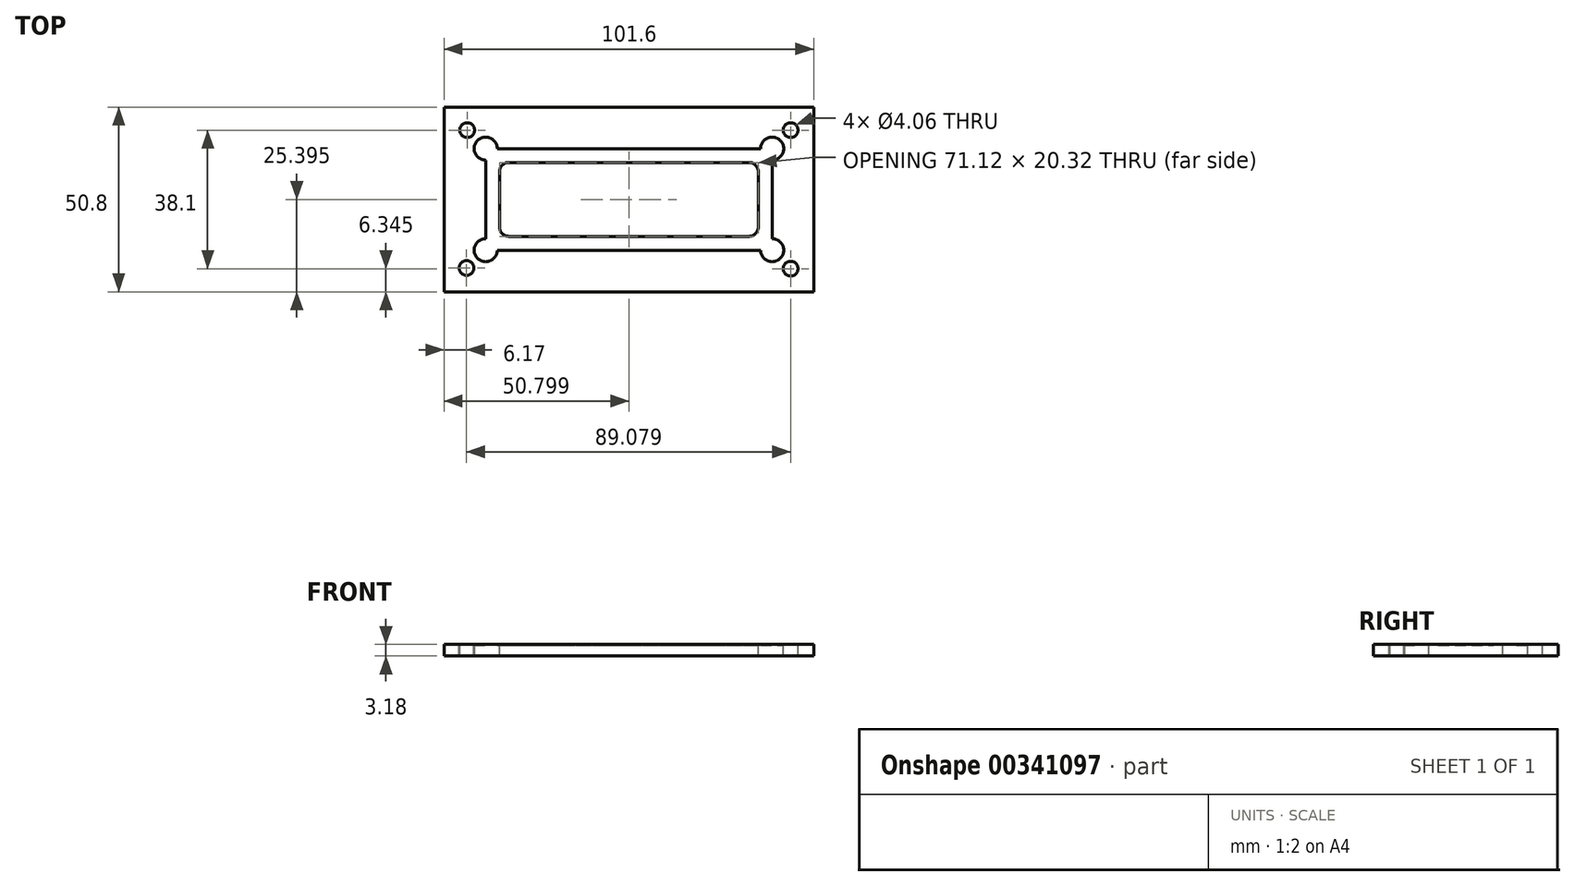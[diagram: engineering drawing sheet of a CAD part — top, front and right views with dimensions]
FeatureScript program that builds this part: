
annotation { "Feature Type Name" : "Feature", "Feature Type Description" : "" }
export const myFeature = defineFeature(function(context is Context, id is Id, definition is map)
    precondition{}
    {
        {
            var Q0;
            Q0=qCreatedBy(makeId("Top.planeOp"),FACE);
            var sketch = newSketch(context, id + "F0", { "sketchPlane" : qUnion([Q0])});
            skLineSegment(sketch, "E0.bottom", {"start": v(0.18, 50.6) * mm, "end": v(101.78, 50.6) * mm});
            skLineSegment(sketch, "E0.top", {"start": v(0.18, -0.2) * mm, "end": v(101.78, -0.2) * mm});
            skLineSegment(sketch, "E0.left", {"start": v(0.18, 50.6) * mm, "end": v(0.18, -0.2) * mm});
            skLineSegment(sketch, "E0.right", {"start": v(101.78, 50.6) * mm, "end": v(101.78, -0.2) * mm});
            skSolve(sketch);
        }
        {
            var Q0;
            Q0=makeQuery(id+"F0.imprint","IMPRINT",FACE,{"disambiguationData":[TD([[makeQuery(id+"F0.imprint","IMPRINT",EDGE,{"derivedFrom":sQuery(id+"F0.wireOp",EDGE,"E0.bottom")}),-1.0]])]});
            extrude(context, id + "F1", {"entities" : qUnion([Q0]), "depth" : 3.17 * mm});
        }
        {
            var Q0;
            Q0=makeQuery(id+"F1.opExtrude","CAP_FACE",FACE,{"disambiguationData":[OSD([sQuery(id+"F0.wireOp",EDGE,"E0.bottom"),sQuery(id+"F0.wireOp",EDGE,"E0.top"),sQuery(id+"F0.wireOp",EDGE,"E0.left"),sQuery(id+"F0.wireOp",EDGE,"E0.right")])],"isStart":false});
            var sketch = newSketch(context, id + "F2", { "sketchPlane" : qUnion([Q0])});
            skLineSegment(sketch, "E1.bottom", {"start": v(11.6, 39.17) * mm, "end": v(90.35, 39.17) * mm});
            skLineSegment(sketch, "E1.top", {"start": v(11.6, 11.23) * mm, "end": v(90.35, 11.23) * mm});
            skLineSegment(sketch, "E1.left", {"start": v(11.6, 39.17) * mm, "end": v(11.6, 11.23) * mm});
            skLineSegment(sketch, "E1.right", {"start": v(90.35, 39.17) * mm, "end": v(90.35, 11.23) * mm});
            skCircle(sketch, "E2", {"center": v(11.6, 39.17) * mm, "radius": 3.18 * mm});
            skCircle(sketch, "E3", {"center": v(11.6, 11.23) * mm, "radius": 3.18 * mm});
            skCircle(sketch, "E4", {"center": v(90.35, 39.17) * mm, "radius": 3.18 * mm});
            skCircle(sketch, "E5", {"center": v(90.35, 11.23) * mm, "radius": 3.18 * mm});
            skSolve(sketch);
        }
        {
            var Q0;
            {var subQ0=sQuery(id+"F2.wireOp",EDGE,"E1.left");var subQ1=sQuery(id+"F2.wireOp",EDGE,"E1.bottom");var subQ2=makeQuery(id+"F2.imprint","INTERSECT",VERTEX,{"derivedFrom":[subQ1,subQ0]});Q0=makeQuery(id+"F2.imprint","IMPRINT",FACE,{"disambiguationData":[TD([[makeQuery(id+"F2.imprint","IMPRINT",EDGE,{"disambiguationData":[TD([[subQ2,-1.0]])],"derivedFrom":subQ1}),1.0]])]});}
            var Q1;
            {var subQ0=sQuery(id+"F2.wireOp",EDGE,"E1.left");var subQ1=sQuery(id+"F2.wireOp",EDGE,"E1.bottom");var subQ2=makeQuery(id+"F2.imprint","INTERSECT",VERTEX,{"derivedFrom":[subQ1,subQ0]});Q1=makeQuery(id+"F2.imprint","IMPRINT",FACE,{"disambiguationData":[TD([[makeQuery(id+"F2.imprint","IMPRINT",EDGE,{"disambiguationData":[TD([[subQ2,-1.0]])],"derivedFrom":subQ1}),-1.0]])]});}
            var Q2;
            {var subQ0=sQuery(id+"F2.wireOp",EDGE,"E1.left");var subQ1=sQuery(id+"F2.wireOp",EDGE,"E1.top");var subQ2=makeQuery(id+"F2.imprint","INTERSECT",VERTEX,{"derivedFrom":[subQ1,subQ0]});Q2=makeQuery(id+"F2.imprint","IMPRINT",FACE,{"disambiguationData":[TD([[makeQuery(id+"F2.imprint","IMPRINT",EDGE,{"disambiguationData":[TD([[subQ2,-1.0]])],"derivedFrom":subQ1}),1.0]])]});}
            var Q3;
            {var subQ0=sQuery(id+"F2.wireOp",EDGE,"E1.left");var subQ1=sQuery(id+"F2.wireOp",EDGE,"E1.top");var subQ2=makeQuery(id+"F2.imprint","INTERSECT",VERTEX,{"derivedFrom":[subQ1,subQ0]});Q3=makeQuery(id+"F2.imprint","IMPRINT",FACE,{"disambiguationData":[TD([[makeQuery(id+"F2.imprint","IMPRINT",EDGE,{"disambiguationData":[TD([[subQ2,-1.0]])],"derivedFrom":subQ1}),-1.0]])]});}
            var Q4;
            {var subQ0=sQuery(id+"F2.wireOp",EDGE,"E1.right");var subQ1=sQuery(id+"F2.wireOp",EDGE,"E1.top");var subQ2=makeQuery(id+"F2.imprint","INTERSECT",VERTEX,{"derivedFrom":[subQ1,subQ0]});Q4=makeQuery(id+"F2.imprint","IMPRINT",FACE,{"disambiguationData":[TD([[makeQuery(id+"F2.imprint","IMPRINT",EDGE,{"disambiguationData":[TD([[subQ2,1.0]])],"derivedFrom":subQ1}),1.0]])]});}
            var Q5;
            {var subQ0=sQuery(id+"F2.wireOp",EDGE,"E1.right");var subQ1=sQuery(id+"F2.wireOp",EDGE,"E1.top");var subQ2=makeQuery(id+"F2.imprint","INTERSECT",VERTEX,{"derivedFrom":[subQ1,subQ0]});Q5=makeQuery(id+"F2.imprint","IMPRINT",FACE,{"disambiguationData":[TD([[makeQuery(id+"F2.imprint","IMPRINT",EDGE,{"disambiguationData":[TD([[subQ2,1.0]])],"derivedFrom":subQ1}),-1.0]])]});}
            var Q6;
            {var subQ0=sQuery(id+"F2.wireOp",EDGE,"E1.right");var subQ1=sQuery(id+"F2.wireOp",EDGE,"E1.bottom");var subQ2=makeQuery(id+"F2.imprint","INTERSECT",VERTEX,{"derivedFrom":[subQ1,subQ0]});Q6=makeQuery(id+"F2.imprint","IMPRINT",FACE,{"disambiguationData":[TD([[makeQuery(id+"F2.imprint","IMPRINT",EDGE,{"disambiguationData":[TD([[subQ2,1.0]])],"derivedFrom":subQ1}),1.0]])]});}
            var Q7;
            {var subQ0=sQuery(id+"F2.wireOp",EDGE,"E1.right");var subQ1=sQuery(id+"F2.wireOp",EDGE,"E1.bottom");var subQ2=makeQuery(id+"F2.imprint","INTERSECT",VERTEX,{"derivedFrom":[subQ1,subQ0]});Q7=makeQuery(id+"F2.imprint","IMPRINT",FACE,{"disambiguationData":[TD([[makeQuery(id+"F2.imprint","IMPRINT",EDGE,{"disambiguationData":[TD([[subQ2,1.0]])],"derivedFrom":subQ1}),-1.0]])]});}
            var Q8;
            {var subQ5=sQuery(id+"F2.wireOp",EDGE,"E2");var subQ13=sQuery(id+"F2.wireOp",EDGE,"E1.bottom");var subQ14=makeQuery(id+"F2.imprint","INTERSECT",VERTEX,{"derivedFrom":[subQ13,subQ5]});Q8=makeQuery(id+"F2.imprint","IMPRINT",FACE,{"disambiguationData":[TD([[makeQuery(id+"F2.imprint","IMPRINT",EDGE,{"disambiguationData":[TD([[subQ14,-1.0]])],"derivedFrom":subQ13}),-1.0]])]});}
            extrude(context, id + "F3", {"entities" : qUnion([Q0, Q1, Q2, Q3, Q4, Q5, Q6, Q7, Q8]), "operationType" : NewBodyOperationType.REMOVE, "oppositeDirection" : true, "depth" : 0.25 * mm});
        }
        {
            var Q0;
            Q0=makeQuery(id+"F3.boolean.opBoolean","COPY",FACE,{"derivedFrom":makeQuery(id+"F3.opExtrude","CAP_FACE",FACE,{"disambiguationData":[OSD([sQuery(id+"F2.wireOp",EDGE,"E1.bottom"),sQuery(id+"F2.wireOp",EDGE,"E1.top"),sQuery(id+"F2.wireOp",EDGE,"E1.left"),sQuery(id+"F2.wireOp",EDGE,"E1.right"),sQuery(id+"F2.wireOp",EDGE,"E2"),sQuery(id+"F2.wireOp",EDGE,"E3"),sQuery(id+"F2.wireOp",EDGE,"E4"),sQuery(id+"F2.wireOp",EDGE,"E5")])],"isStart":false})});
            var sketch = newSketch(context, id + "F4", { "sketchPlane" : qUnion([Q0])});
            skLineSegment(sketch, "E6.bottom", {"start": v(17.96, 15.04) * mm, "end": v(84, 15.04) * mm});
            skLineSegment(sketch, "E6.top", {"start": v(17.96, 35.36) * mm, "end": v(84, 35.36) * mm});
            skLineSegment(sketch, "E6.left", {"start": v(15.42, 17.58) * mm, "end": v(15.42, 32.82) * mm});
            skLineSegment(sketch, "E6.right", {"start": v(86.54, 17.58) * mm, "end": v(86.54, 32.82) * mm});
            skPoint(sketch, "E7.visualSharp", {"position": v(86.54, 35.36) * mm});
            skArc(sketch, "E7.filletArc", {"start": v(86.54, 32.82) * mm, "mid": v(85.8, 34.61) * mm, "end": v(84, 35.36) * mm});
            skPoint(sketch, "E8.visualSharp", {"position": v(86.54, 15.04) * mm});
            skArc(sketch, "E8.filletArc", {"start": v(84, 15.04) * mm, "mid": v(85.8, 15.78) * mm, "end": v(86.54, 17.58) * mm});
            skPoint(sketch, "E9.visualSharp", {"position": v(15.42, 15.04) * mm});
            skArc(sketch, "E9.filletArc", {"start": v(15.42, 17.58) * mm, "mid": v(16.16, 15.78) * mm, "end": v(17.96, 15.04) * mm});
            skPoint(sketch, "E10.visualSharp", {"position": v(15.42, 35.36) * mm});
            skArc(sketch, "E10.filletArc", {"start": v(17.96, 35.36) * mm, "mid": v(16.16, 34.61) * mm, "end": v(15.42, 32.82) * mm});
            skSolve(sketch);
        }
        {
            var Q0;
            Q0=qSketchRegion(id+"F4",true);
            extrude(context, id + "F5", {"entities" : qUnion([Q0]), "operationType" : NewBodyOperationType.REMOVE, "oppositeDirection" : true, "depth" : 25.4 * mm, "hasSecondDirection" : true, "secondDirectionOppositeDirection" : false, "secondDirectionDepth" : 25.4 * mm});
        }
        {
            var Q0;
            Q0=makeQuery(id+"F1.opExtrude","CAP_FACE",FACE,{"disambiguationData":[OSD([sQuery(id+"F0.wireOp",EDGE,"E0.bottom"),sQuery(id+"F0.wireOp",EDGE,"E0.top"),sQuery(id+"F0.wireOp",EDGE,"E0.left"),sQuery(id+"F0.wireOp",EDGE,"E0.right")])],"isStart":false});
            var sketch = newSketch(context, id + "F6", { "sketchPlane" : qUnion([Q0])});
            skCircle(sketch, "E11", {"center": v(6.53, 44.25) * mm, "radius": 2.03 * mm});
            skCircle(sketch, "E12", {"center": v(95.43, 44.25) * mm, "radius": 2.03 * mm});
            skCircle(sketch, "E13", {"center": v(95.43, 6.15) * mm, "radius": 2.03 * mm});
            skCircle(sketch, "E14", {"center": v(6.35, 6.35) * mm, "radius": 2.03 * mm});
            skSolve(sketch);
        }
        {
            var Q0;
            Q0=makeQuery(id+"F6.imprint","IMPRINT",FACE,{"disambiguationData":[TD([[makeQuery(id+"F6.imprint","IMPRINT",EDGE,{"derivedFrom":sQuery(id+"F6.wireOp",EDGE,"E11")}),1.0]])]});
            var Q1;
            Q1=makeQuery(id+"F6.imprint","IMPRINT",FACE,{"disambiguationData":[TD([[makeQuery(id+"F6.imprint","IMPRINT",EDGE,{"derivedFrom":sQuery(id+"F6.wireOp",EDGE,"E12")}),1.0]])]});
            var Q2;
            Q2=makeQuery(id+"F6.imprint","IMPRINT",FACE,{"disambiguationData":[TD([[makeQuery(id+"F6.imprint","IMPRINT",EDGE,{"derivedFrom":sQuery(id+"F6.wireOp",EDGE,"E13")}),1.0]])]});
            var Q3;
            Q3=makeQuery(id+"F6.imprint","IMPRINT",FACE,{"disambiguationData":[TD([[makeQuery(id+"F6.imprint","IMPRINT",EDGE,{"derivedFrom":sQuery(id+"F6.wireOp",EDGE,"E14")}),1.0]])]});
            extrude(context, id + "F7", {"entities" : qUnion([Q0, Q1, Q2, Q3]), "operationType" : NewBodyOperationType.REMOVE, "oppositeDirection" : true, "depth" : 25.4 * mm, "hasSecondDirection" : true, "secondDirectionOppositeDirection" : false, "secondDirectionDepth" : 25.4 * mm});
        }
    });
